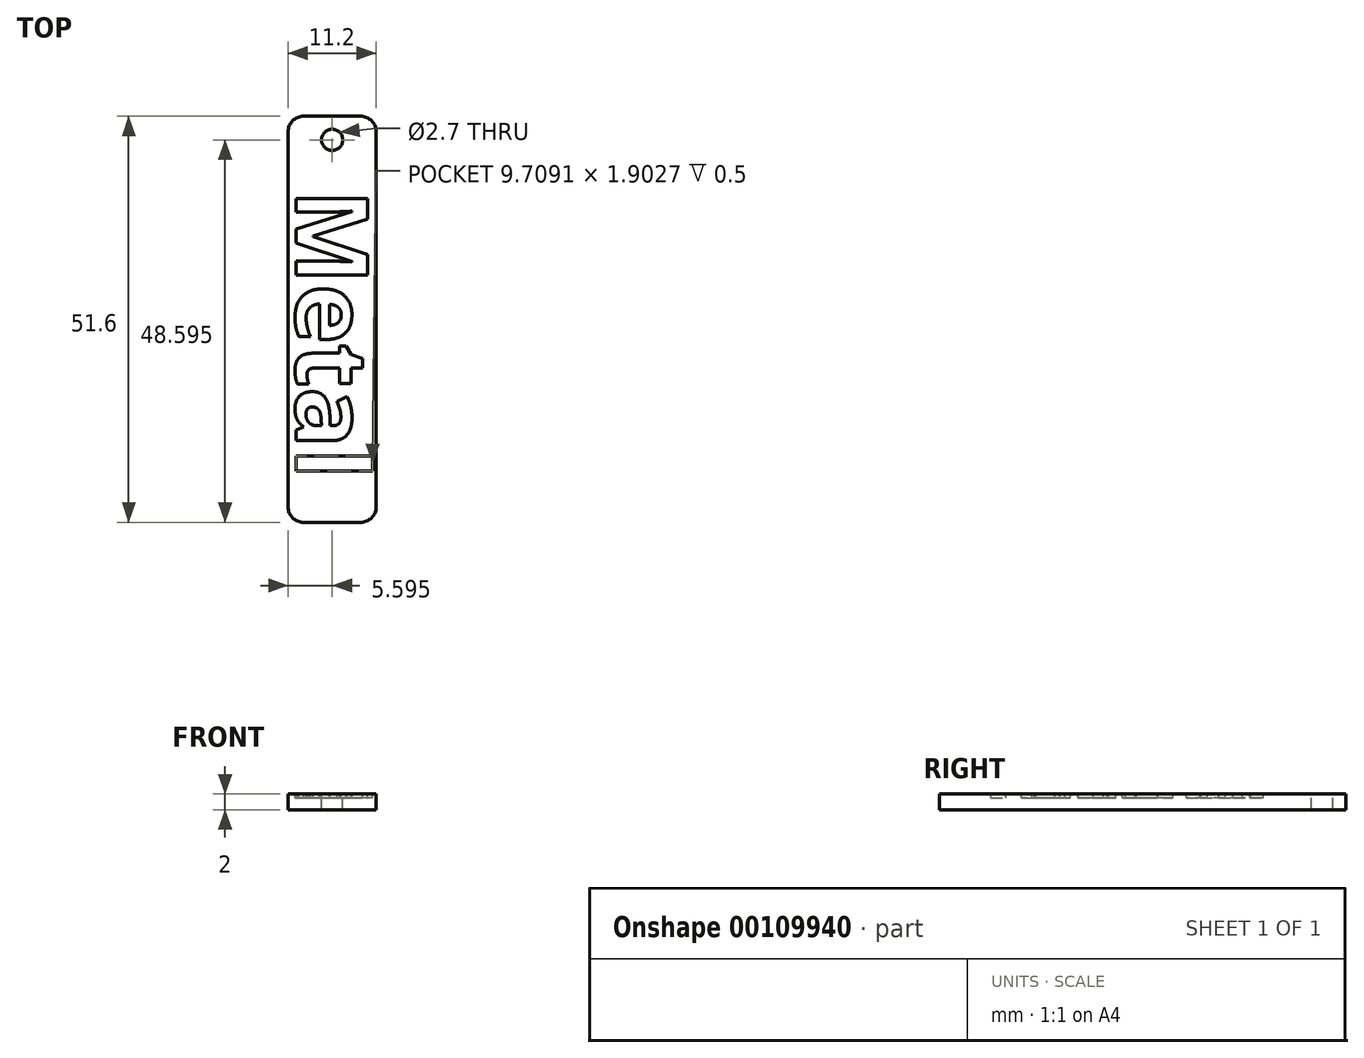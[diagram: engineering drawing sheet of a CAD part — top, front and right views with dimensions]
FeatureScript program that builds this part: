
annotation { "Feature Type Name" : "Feature", "Feature Type Description" : "" }
export const myFeature = defineFeature(function(context is Context, id is Id, definition is map)
    precondition{}
    {
        {
            var Q0;
            Q0=qCreatedBy(makeId("Top.planeOp"),FACE);
            var sketch = newSketch(context, id + "F0", { "sketchPlane" : qUnion([Q0])});
            skLineSegment(sketch, "E0.bottom", {"start": v(-49.26, 74.45) * mm, "end": v(-38.06, 74.45) * mm});
            skLineSegment(sketch, "E0.top", {"start": v(-49.26, 22.85) * mm, "end": v(-38.06, 22.85) * mm});
            skLineSegment(sketch, "E0.left", {"start": v(-49.26, 74.45) * mm, "end": v(-49.26, 22.85) * mm});
            skLineSegment(sketch, "E0.right", {"start": v(-38.06, 74.45) * mm, "end": v(-38.06, 22.85) * mm});
            skCircle(sketch, "E1", {"center": v(-43.66, 71.45) * mm, "radius": 1.35 * mm});
            skText(sketch, "E2", { "text": "Metal", "fontName": "OpenSans-Bold.ttf"});
            const initialGuessF0  = {"E2": [-0.04826, 0.06514, 0, -1, 0.0092]};
            skSetInitialGuess(sketch, initialGuessF0);
            skSolve(sketch);
        }
        {
            var Q0;
            Q0=makeQuery(id+"F0.imprint","IMPRINT",FACE,{"disambiguationData":[TD([[makeQuery(id+"F0.imprint","IMPRINT",EDGE,{"derivedFrom":sQuery(id+"F0.wireOp",EDGE,"E2.sketch_text.stroke-8")}),1.0]])]});
            var Q1;
            Q1=makeQuery(id+"F0.imprint","IMPRINT",FACE,{"disambiguationData":[TD([[makeQuery(id+"F0.imprint","IMPRINT",EDGE,{"derivedFrom":sQuery(id+"F0.wireOp",EDGE,"E2.sketch_text.stroke-14")}),-1.0]])]});
            var Q2;
            Q2=makeQuery(id+"F0.imprint","IMPRINT",FACE,{"disambiguationData":[TD([[makeQuery(id+"F0.imprint","IMPRINT",EDGE,{"derivedFrom":sQuery(id+"F0.wireOp",EDGE,"E2.sketch_text.stroke-32")}),-1.0]])]});
            var Q3;
            Q3=makeQuery(id+"F0.imprint","IMPRINT",FACE,{"disambiguationData":[TD([[makeQuery(id+"F0.imprint","IMPRINT",EDGE,{"derivedFrom":sQuery(id+"F0.wireOp",EDGE,"E2.sketch_text.stroke-49")}),-1.0]])]});
            var Q4;
            Q4=makeQuery(id+"F0.imprint","IMPRINT",FACE,{"disambiguationData":[TD([[makeQuery(id+"F0.imprint","IMPRINT",EDGE,{"derivedFrom":sQuery(id+"F0.wireOp",EDGE,"E2.sketch_text.stroke-69")}),-1.0]])]});
            var Q5;
            Q5=makeQuery(id+"F0.imprint","IMPRINT",FACE,{"disambiguationData":[TD([[makeQuery(id+"F0.imprint","IMPRINT",EDGE,{"derivedFrom":sQuery(id+"F0.wireOp",EDGE,"E0.bottom")}),-1.0]])]});
            var Q6;
            Q6=makeQuery(id+"F0.imprint","IMPRINT",FACE,{"disambiguationData":[TD([[makeQuery(id+"F0.imprint","IMPRINT",EDGE,{"derivedFrom":sQuery(id+"F0.wireOp",EDGE,"E2.sketch_text.stroke-0")}),-1.0]])]});
            var Q7;
            Q7=makeQuery(id+"F0.imprint","IMPRINT",FACE,{"disambiguationData":[TD([[makeQuery(id+"F0.imprint","IMPRINT",EDGE,{"derivedFrom":sQuery(id+"F0.wireOp",EDGE,"E2.sketch_text.stroke-49")}),1.0]])]});
            var Q8;
            Q8=makeQuery(id+"F0.imprint","IMPRINT",FACE,{"disambiguationData":[TD([[makeQuery(id+"F0.imprint","IMPRINT",EDGE,{"derivedFrom":sQuery(id+"F0.wireOp",EDGE,"E2.sketch_text.stroke-19")}),1.0]])]});
            var Q9;
            Q9=makeQuery(id+"F0.imprint","IMPRINT",FACE,{"disambiguationData":[TD([[makeQuery(id+"F0.imprint","IMPRINT",EDGE,{"derivedFrom":sQuery(id+"F0.wireOp",EDGE,"E2.sketch_text.stroke-75")}),1.0]])]});
            var Q10;
            Q10=makeQuery(id+"F0.imprint","IMPRINT",FACE,{"disambiguationData":[TD([[makeQuery(id+"F0.imprint","IMPRINT",EDGE,{"derivedFrom":sQuery(id+"F0.wireOp",EDGE,"E2.sketch_text.stroke-82")}),-1.0]])]});
            extrude(context, id + "F1", {"entities" : qUnion([Q0, Q1, Q2, Q3, Q4, Q5, Q6, Q7, Q8, Q9, Q10]), "oppositeDirection" : true, "depth" : 2 * mm});
        }
        {
            var Q0;
            Q0=makeQuery(id+"F0.imprint","IMPRINT",FACE,{"disambiguationData":[TD([[makeQuery(id+"F0.imprint","IMPRINT",EDGE,{"derivedFrom":sQuery(id+"F0.wireOp",EDGE,"E2.sketch_text.stroke-0")}),-1.0]])]});
            var Q1;
            Q1=makeQuery(id+"F0.imprint","IMPRINT",FACE,{"disambiguationData":[TD([[makeQuery(id+"F0.imprint","IMPRINT",EDGE,{"derivedFrom":sQuery(id+"F0.wireOp",EDGE,"E2.sketch_text.stroke-16")}),-1.0]])]});
            var Q2;
            Q2=makeQuery(id+"F0.imprint","IMPRINT",FACE,{"disambiguationData":[TD([[makeQuery(id+"F0.imprint","IMPRINT",EDGE,{"derivedFrom":sQuery(id+"F0.wireOp",EDGE,"E2.sketch_text.stroke-28")}),-1.0]])]});
            var Q3;
            Q3=makeQuery(id+"F0.imprint","IMPRINT",FACE,{"disambiguationData":[TD([[makeQuery(id+"F0.imprint","IMPRINT",EDGE,{"derivedFrom":sQuery(id+"F0.wireOp",EDGE,"E2.sketch_text.stroke-36")}),-1.0]])]});
            var Q4;
            Q4=makeQuery(id+"F0.imprint","IMPRINT",FACE,{"disambiguationData":[TD([[makeQuery(id+"F0.imprint","IMPRINT",EDGE,{"derivedFrom":sQuery(id+"F0.wireOp",EDGE,"E2.sketch_text.stroke-49")}),-1.0]])]});
            var Q5;
            Q5=makeQuery(id+"F0.imprint","IMPRINT",FACE,{"disambiguationData":[TD([[makeQuery(id+"F0.imprint","IMPRINT",EDGE,{"derivedFrom":sQuery(id+"F0.wireOp",EDGE,"E2.sketch_text.stroke-69")}),-1.0]])]});
            var Q6;
            Q6=makeQuery(id+"F0.imprint","IMPRINT",FACE,{"disambiguationData":[TD([[makeQuery(id+"F0.imprint","IMPRINT",EDGE,{"derivedFrom":sQuery(id+"F0.wireOp",EDGE,"E2.sketch_text.stroke-82")}),-1.0]])]});
            var Q7;
            Q7=qConstructionFilter(qBodyType(qCreatedBy(id+"F0",EDGE),BodyType.WIRE),ConstructionObject.NO);
            extrude(context, id + "F2", {"entities" : qUnion([Q0, Q1, Q2, Q3, Q4, Q5, Q6]), "operationType" : NewBodyOperationType.REMOVE, "surfaceEntities" : qUnion([Q7]), "oppositeDirection" : true, "depth" : .5 * mm});
        }
        {
            var Q0;
            Q0=makeQuery(id+"F1.opExtrude","SWEPT_EDGE",EDGE,{"disambiguationData":[OSD([sQuery(id+"F0.wireOp",EDGE,"E0.bottom"),sQuery(id+"F0.wireOp",EDGE,"E0.left")])]});
            var Q1;
            Q1=makeQuery(id+"F1.opExtrude","SWEPT_EDGE",EDGE,{"disambiguationData":[OSD([sQuery(id+"F0.wireOp",EDGE,"E0.bottom"),sQuery(id+"F0.wireOp",EDGE,"E0.right")])]});
            var Q2;
            Q2=makeQuery(id+"F1.opExtrude","SWEPT_EDGE",EDGE,{"disambiguationData":[OSD([sQuery(id+"F0.wireOp",EDGE,"E0.top"),sQuery(id+"F0.wireOp",EDGE,"E0.right")])]});
            var Q3;
            Q3=makeQuery(id+"F1.opExtrude","SWEPT_EDGE",EDGE,{"disambiguationData":[OSD([sQuery(id+"F0.wireOp",EDGE,"E0.top"),sQuery(id+"F0.wireOp",EDGE,"E0.left")])]});
            fillet(context, id + "F3", {"entities" : qUnion([Q0, Q1, Q2, Q3]), "radius" : 2 * mm, "tangentPropagation" : true, "allowEdgeOverflow" : false});
        }
    });
